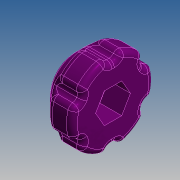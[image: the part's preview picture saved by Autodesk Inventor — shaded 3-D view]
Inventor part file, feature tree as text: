
AUTODESK INVENTOR PART (.ipt)
format: ipt  version: 2019 (Build 230136000, 136)  size: 548,864 bytes
history: native  units: mm
features: sketch x3, extrude x2, fillet x2, revolve x1, mirror x1, pattern_circular x1
ambient origin geometry x8: Origin, YZ Plane, XZ Plane, XY Plane, X Axis, Y Axis, Z Axis, Center Point
bodies: Solid1 (feature_tree)
feature tree (10):
  revolve  "Revolution1"  Angle=45.0deg
  extrude  "Extrusion1"  Depth=4.0mm
  extrude  "Extrusion2"  TaperAngle=90.0deg  [1 undecoded]
  fillet  "Fillet1"  Radius=5.5mm
  mirror  "Mirror1"
  pattern_circular  "Circular Pattern1"  [2 undecoded]
  fillet  "Fillet2"  Radius=1.308997mm
  sketch  "Sketch1"  dims[d0=3.3mm d1=45.0deg]
  sketch  "Sketch2"  dims[d2=15.0mm d3=4.0mm]
  sketch  "Sketch3"  dims[d4=7.0mm d5=90.0deg d6=5.5mm d7=4.0mm d8=0.0mm d9=1.308997mm d10=1.0mm d11=4.0mm d12=0.0mm d13=1.0mm d14=60.0mm d15=360.0deg d17=1.0mm]
note: 3 required parameter values undecoded (feature->parameter linkage not recoverable at this tier; creation-order binding heuristic only, values carry confidence <= 0.55)
